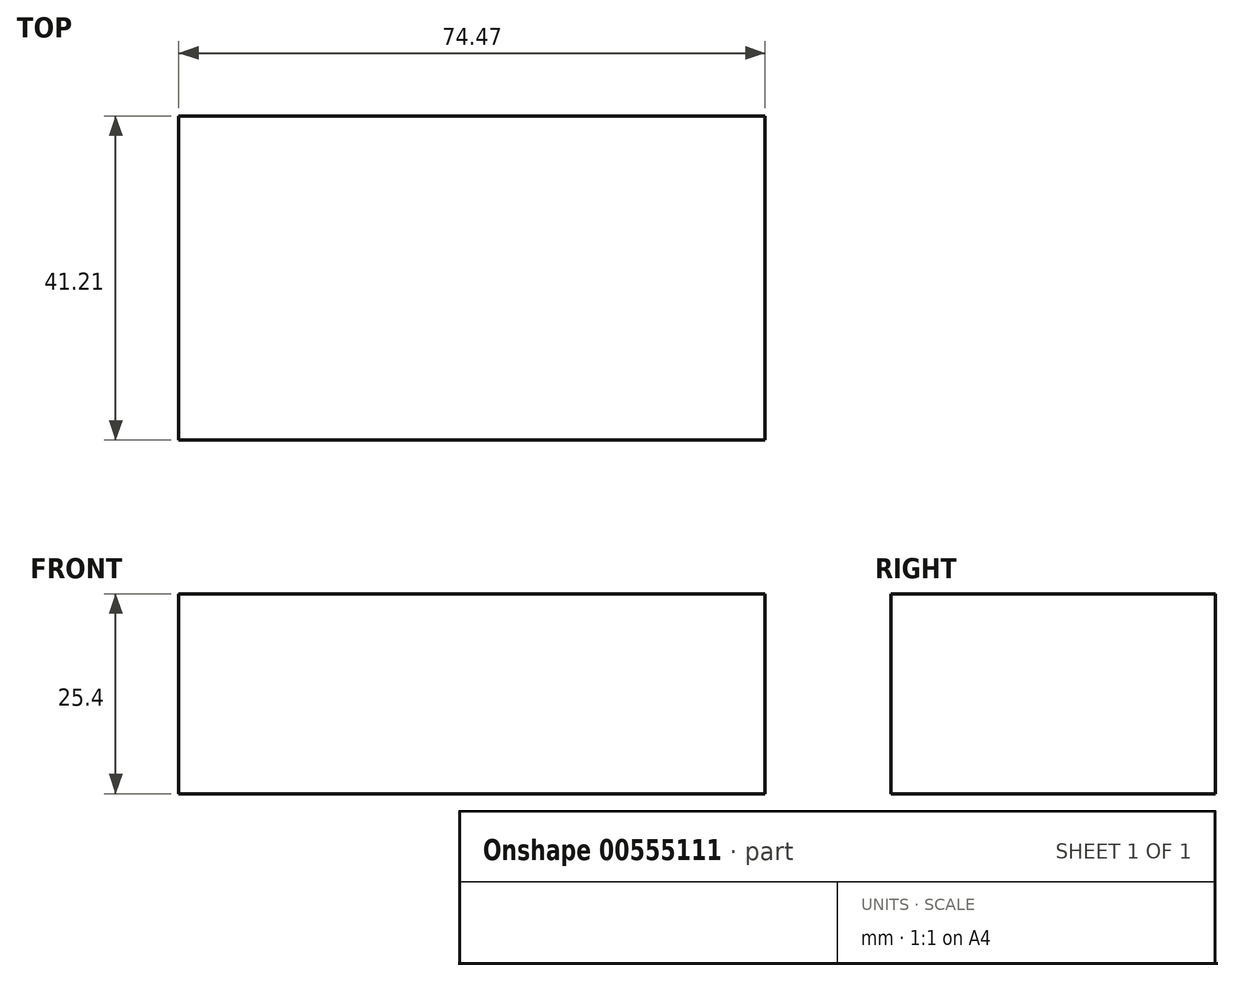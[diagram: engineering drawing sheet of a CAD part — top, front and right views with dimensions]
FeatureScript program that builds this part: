
annotation { "Feature Type Name" : "Feature", "Feature Type Description" : "" }
export const myFeature = defineFeature(function(context is Context, id is Id, definition is map)
    precondition{}
    {
        {
            var Q0;
            Q0=qCreatedBy(makeId("Top.planeOp"),FACE);
            var sketch = newSketch(context, id + "F0", { "sketchPlane" : qUnion([Q0])});
            skLineSegment(sketch, "E0.bottom", {"start": v(0, 0) * mm, "end": v(74.47, 0) * mm});
            skLineSegment(sketch, "E0.top", {"start": v(0, 41.2) * mm, "end": v(74.47, 41.2) * mm});
            skLineSegment(sketch, "E0.left", {"start": v(0, 0) * mm, "end": v(0, 41.2) * mm});
            skLineSegment(sketch, "E0.right", {"start": v(74.47, 0) * mm, "end": v(74.47, 41.2) * mm});
            skSolve(sketch);
        }
        {
            var Q0;
            Q0=makeQuery(id+"F0.imprint","IMPRINT",FACE,{"disambiguationData":[TD([[makeQuery(id+"F0.imprint","IMPRINT",EDGE,{"derivedFrom":sQuery(id+"F0.wireOp",EDGE,"E0.bottom")}),1.0]])]});
            extrude(context, id + "F1", {"entities" : qUnion([Q0]), "depth" : 25.4 * mm, "offsetDistance" : 25.4 * mm});
        }
    });
